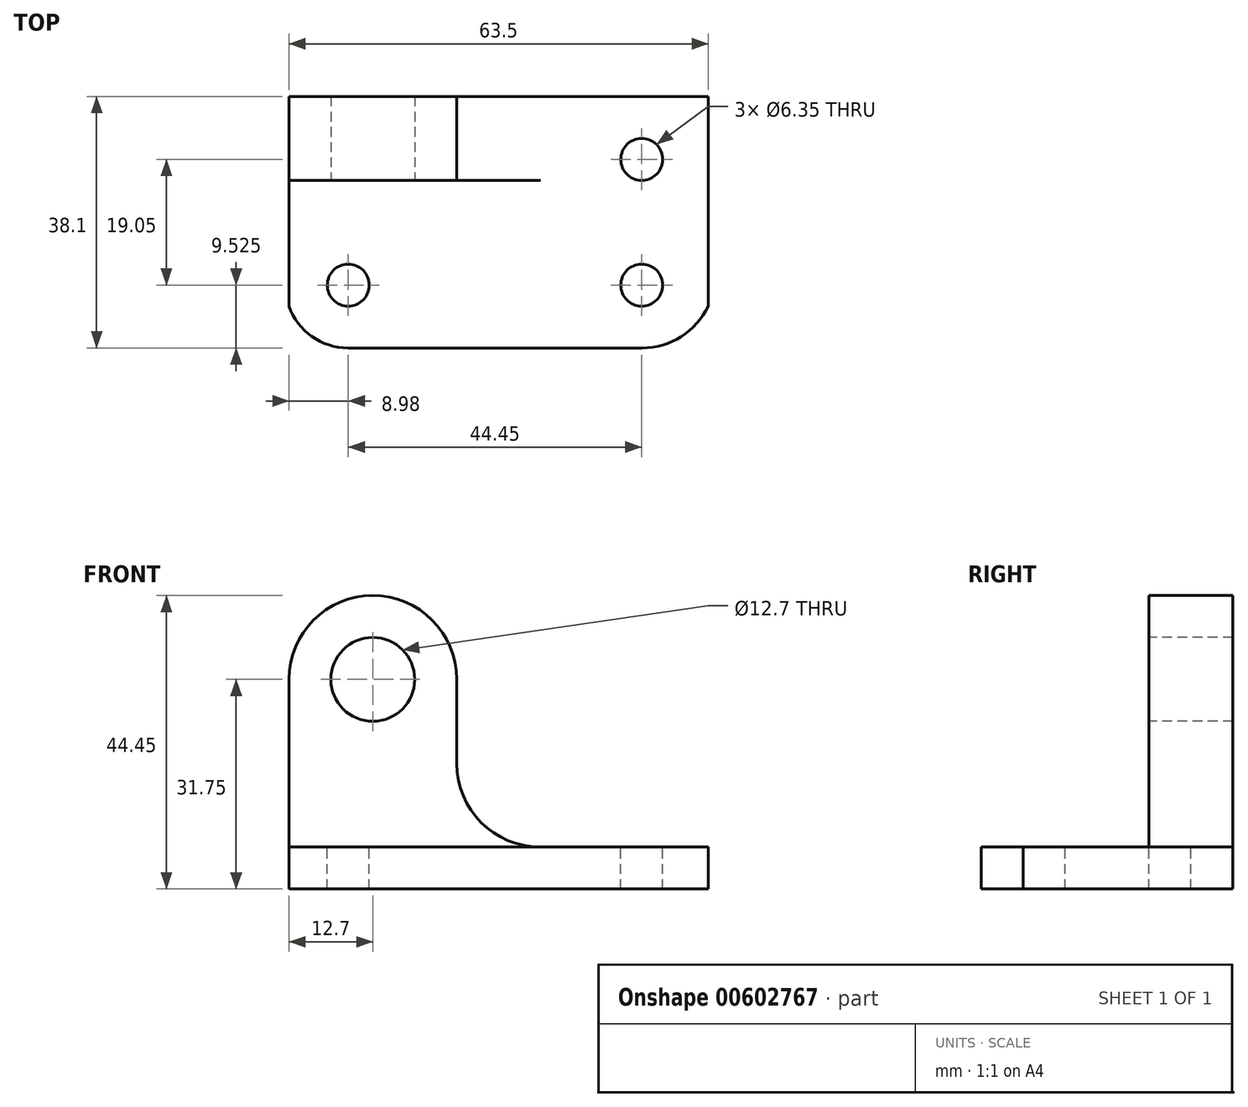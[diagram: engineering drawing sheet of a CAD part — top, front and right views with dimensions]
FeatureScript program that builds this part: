
annotation { "Feature Type Name" : "Feature", "Feature Type Description" : "" }
export const myFeature = defineFeature(function(context is Context, id is Id, definition is map)
    precondition{}
    {
        {
            var Q0;
            Q0=qCreatedBy(makeId("Front.planeOp"),FACE);
            var sketch = newSketch(context, id + "F0", { "sketchPlane" : qUnion([Q0])});
            skLineSegment(sketch, "E0", {"start": v(0, 0) * mm, "end": v(63.5, 0) * mm});
            skLineSegment(sketch, "E1", {"start": v(63.5, 0) * mm, "end": v(63.5, 6.35) * mm});
            skLineSegment(sketch, "E2", {"start": v(63.5, 6.35) * mm, "end": v(38.1, 6.35) * mm});
            skLineSegment(sketch, "E3", {"start": v(38.1, 6.35) * mm, "end": v(38.1, 44.45) * mm});
            skLineSegment(sketch, "E4", {"start": v(38.1, 44.45) * mm, "end": v(0, 44.45) * mm});
            skLineSegment(sketch, "E5", {"start": v(0, 44.45) * mm, "end": v(0, 0) * mm});
            skSolve(sketch);
        }
        {
            var Q0;
            Q0=makeQuery(id+"F0.imprint","IMPRINT",FACE,{"disambiguationData":[TD([[makeQuery(id+"F0.imprint","IMPRINT",EDGE,{"derivedFrom":sQuery(id+"F0.wireOp",EDGE,"E0")}),1.0]])]});
            var sketch = newSketch(context, id + "F1", { "sketchPlane" : qUnion([Q0])});
            skLineSegment(sketch, "E6.0.0", {"start": v(38.1, 44.45) * mm, "end": v(0, 44.45) * mm});
            skLineSegment(sketch, "E6.0.1", {"start": v(0, 44.45) * mm, "end": v(0, 0) * mm});
            skLineSegment(sketch, "E6.0.2", {"start": v(0, 0) * mm, "end": v(63.5, 0) * mm});
            skLineSegment(sketch, "E6.0.3", {"start": v(63.5, 0) * mm, "end": v(63.5, 6.35) * mm});
            skLineSegment(sketch, "E6.0.4", {"start": v(63.5, 6.35) * mm, "end": v(38.1, 6.35) * mm});
            skLineSegment(sketch, "E6.0.5", {"start": v(38.1, 6.35) * mm, "end": v(38.1, 44.45) * mm});
            skArc(sketch, "E7", {"start": v(25.4, 31.75) * mm, "mid": v(12.7, 44.45) * mm, "end": v(0, 31.75) * mm});
            skLineSegment(sketch, "E8", {"start": v(25.4, 31.75) * mm, "end": v(25.4, 19.05) * mm});
            skArc(sketch, "E9", {"start": v(25.4, 19.05) * mm, "mid": v(29.12, 10.07) * mm, "end": v(38.1, 6.35) * mm});
            skSolve(sketch);
        }
        {
            var Q0;
            Q0=makeQuery(id+"F0.imprint","IMPRINT",FACE,{"disambiguationData":[TD([[makeQuery(id+"F0.imprint","IMPRINT",EDGE,{"derivedFrom":sQuery(id+"F0.wireOp",EDGE,"E0")}),1.0]])]});
            var sketch = newSketch(context, id + "F2", { "sketchPlane" : qUnion([Q0])});
            skLineSegment(sketch, "E10.0.0", {"start": v(38.1, 44.45) * mm, "end": v(0, 44.45) * mm});
            skLineSegment(sketch, "E10.0.1", {"start": v(0, 44.45) * mm, "end": v(0, 0) * mm});
            skLineSegment(sketch, "E10.0.2", {"start": v(0, 0) * mm, "end": v(63.5, 0) * mm});
            skLineSegment(sketch, "E10.0.3", {"start": v(63.5, 0) * mm, "end": v(63.5, 6.35) * mm});
            skLineSegment(sketch, "E10.0.4", {"start": v(63.5, 6.35) * mm, "end": v(38.1, 6.35) * mm});
            skLineSegment(sketch, "E10.0.5", {"start": v(38.1, 6.35) * mm, "end": v(38.1, 44.45) * mm});
            skLineSegment(sketch, "E11", {"start": v(38.1, 6.35) * mm, "end": v(0, 6.35) * mm});
            skSolve(sketch);
        }
        {
            var Q0;
            Q0=makeQuery(id+"F0.imprint","IMPRINT",FACE,{"disambiguationData":[TD([[makeQuery(id+"F0.imprint","IMPRINT",EDGE,{"derivedFrom":sQuery(id+"F0.wireOp",EDGE,"E0")}),1.0]])]});
            extrude(context, id + "F3", {"entities" : qUnion([Q0]), "oppositeDirection" : true, "depth" : 38.1 * mm, "offsetDistance" : 25.4 * mm});
        }
        {
            var Q0;
            {var subQ4=sQuery(id+"F1.wireOp",EDGE,"E6.0.5");Q0=makeQuery(id+"F1.imprint","IMPRINT",FACE,{"disambiguationData":[TD([[makeQuery(id+"F1.imprint","IMPRINT",EDGE,{"derivedFrom":subQ4}),1.0]])]});}
            var Q1;
            {var subQ0=sQuery(id+"F1.wireOp",EDGE,"E6.0.1");var subQ1=sQuery(id+"F1.wireOp",EDGE,"E6.0.0");var subQ2=makeQuery(id+"F1.imprint","INTERSECT",VERTEX,{"derivedFrom":[subQ1,subQ0]});Q1=makeQuery(id+"F1.imprint","IMPRINT",FACE,{"disambiguationData":[TD([[makeQuery(id+"F1.imprint","IMPRINT",EDGE,{"disambiguationData":[TD([[subQ2,1.0]])],"derivedFrom":subQ1}),1.0]])]});}
            extrude(context, id + "F4", {"entities" : qUnion([Q0, Q1]), "operationType" : NewBodyOperationType.REMOVE, "oppositeDirection" : true, "depth" : 38.1 * mm, "offsetDistance" : 25.4 * mm});
        }
        {
            var Q0;
            {var subQ0=sQuery(id+"F2.wireOp",EDGE,"E10.0.0");Q0=makeQuery(id+"F2.imprint","IMPRINT",FACE,{"disambiguationData":[TD([[makeQuery(id+"F2.imprint","IMPRINT",EDGE,{"derivedFrom":subQ0}),1.0]])]});}
            extrude(context, id + "F5", {"entities" : qUnion([Q0]), "operationType" : NewBodyOperationType.REMOVE, "oppositeDirection" : true, "depth" : 25.4 * mm, "offsetDistance" : 25.4 * mm});
        }
        {
            var Q0;
            Q0=makeQuery(id+"F5.boolean.opBoolean","MERGE",FACE,{"derivedFrom":[makeQuery(id+"F3.opExtrude","SWEPT_FACE",FACE,{"disambiguationData":[OSD([sQuery(id+"F0.wireOp",EDGE,"E2")])]}),makeQuery(id+"F5.opExtrude","SWEPT_FACE",FACE,{"disambiguationData":[OSD([sQuery(id+"F2.wireOp",EDGE,"E11")])]})]});
            var sketch = newSketch(context, id + "F6", { "sketchPlane" : qUnion([Q0])});
            skLineSegment(sketch, "E12.0.0", {"start": v(0, 0) * mm, "end": v(63.5, 0) * mm});
            skLineSegment(sketch, "E12.0.1", {"start": v(63.5, 0) * mm, "end": v(63.5, 38.1) * mm});
            skLineSegment(sketch, "E12.0.2", {"start": v(63.5, 38.1) * mm, "end": v(38.1, 38.1) * mm});
            skLineSegment(sketch, "E12.0.3", {"start": v(38.1, 38.1) * mm, "end": v(38.1, 25.4) * mm});
            skLineSegment(sketch, "E12.0.4", {"start": v(38.1, 25.4) * mm, "end": v(0, 25.4) * mm});
            skLineSegment(sketch, "E12.0.5", {"start": v(0, 25.4) * mm, "end": v(0, 0) * mm});
            skArc(sketch, "E13", {"start": v(0, 6.35) * mm, "mid": v(3.46, 1.76) * mm, "end": v(8.94, 0) * mm});
            skArc(sketch, "E14", {"start": v(53.39, 0) * mm, "mid": v(59.36, 1.7) * mm, "end": v(63.5, 6.35) * mm});
            skSolve(sketch);
        }
        {
            var Q0;
            {var subQ3=sQuery(id+"F6.wireOp",EDGE,"E13");Q0=makeQuery(id+"F6.imprint","IMPRINT",FACE,{"disambiguationData":[TD([[makeQuery(id+"F6.imprint","IMPRINT",EDGE,{"derivedFrom":subQ3}),-1.0]])]});}
            var Q1;
            {var subQ0=sQuery(id+"F6.wireOp",EDGE,"E12.0.1");var subQ1=sQuery(id+"F6.wireOp",EDGE,"E12.0.0");var subQ2=makeQuery(id+"F6.imprint","INTERSECT",VERTEX,{"derivedFrom":[subQ1,subQ0]});Q1=makeQuery(id+"F6.imprint","IMPRINT",FACE,{"disambiguationData":[TD([[makeQuery(id+"F6.imprint","IMPRINT",EDGE,{"disambiguationData":[TD([[subQ2,-1.0]])],"derivedFrom":subQ1}),-1.0]])]});}
            extrude(context, id + "F7", {"entities" : qUnion([Q0, Q1]), "operationType" : NewBodyOperationType.REMOVE, "oppositeDirection" : true, "depth" : 6.35 * mm, "offsetDistance" : 25.4 * mm});
        }
        {
            var Q0;
            Q0=makeQuery(id+"F5.boolean.opBoolean","COPY",FACE,{"derivedFrom":makeQuery(id+"F5.opExtrude","CAP_FACE",FACE,{"disambiguationData":[OSD([sQuery(id+"F2.wireOp",EDGE,"E10.0.0"),sQuery(id+"F2.wireOp",EDGE,"E10.0.1"),sQuery(id+"F2.wireOp",EDGE,"E10.0.5"),sQuery(id+"F2.wireOp",EDGE,"E11")])],"isStart":false})});
            var sketch = newSketch(context, id + "F8", { "sketchPlane" : qUnion([Q0])});
            skCircle(sketch, "E15", {"center": v(12.7, 31.75) * mm, "radius": 6.35 * mm});
            skSolve(sketch);
        }
        {
            var Q0;
            Q0=makeQuery(id+"F8.imprint","IMPRINT",FACE,{"disambiguationData":[TD([[makeQuery(id+"F8.imprint","IMPRINT",EDGE,{"derivedFrom":sQuery(id+"F8.wireOp",EDGE,"E15")}),1.0]])]});
            extrude(context, id + "F9", {"entities" : qUnion([Q0]), "operationType" : NewBodyOperationType.REMOVE, "oppositeDirection" : true, "depth" : 12.7 * mm, "offsetDistance" : 25.4 * mm});
        }
        {
            var Q0;
            Q0=makeQuery(id+"F5.boolean.opBoolean","MERGE",FACE,{"derivedFrom":[makeQuery(id+"F3.opExtrude","SWEPT_FACE",FACE,{"disambiguationData":[OSD([sQuery(id+"F0.wireOp",EDGE,"E2")])]}),makeQuery(id+"F5.opExtrude","SWEPT_FACE",FACE,{"disambiguationData":[OSD([sQuery(id+"F2.wireOp",EDGE,"E11")])]})]});
            var sketch = newSketch(context, id + "F10", { "sketchPlane" : qUnion([Q0])});
            skCircle(sketch, "E16", {"center": v(8.98, 9.52) * mm, "radius": 3.17 * mm});
            skCircle(sketch, "E17", {"center": v(53.43, 9.52) * mm, "radius": 3.18 * mm});
            skCircle(sketch, "E18", {"center": v(53.43, 28.58) * mm, "radius": 3.18 * mm});
            skSolve(sketch);
        }
        {
            var Q0;
            Q0=makeQuery(id+"F10.imprint","IMPRINT",FACE,{"disambiguationData":[TD([[makeQuery(id+"F10.imprint","IMPRINT",EDGE,{"derivedFrom":sQuery(id+"F10.wireOp",EDGE,"E16")}),1.0]])]});
            var Q1;
            Q1=makeQuery(id+"F10.imprint","IMPRINT",FACE,{"disambiguationData":[TD([[makeQuery(id+"F10.imprint","IMPRINT",EDGE,{"derivedFrom":sQuery(id+"F10.wireOp",EDGE,"E17")}),1.0]])]});
            var Q2;
            Q2=makeQuery(id+"F10.imprint","IMPRINT",FACE,{"disambiguationData":[TD([[makeQuery(id+"F10.imprint","IMPRINT",EDGE,{"derivedFrom":sQuery(id+"F10.wireOp",EDGE,"E18")}),1.0]])]});
            extrude(context, id + "F11", {"entities" : qUnion([Q0, Q1, Q2]), "operationType" : NewBodyOperationType.REMOVE, "oppositeDirection" : true, "depth" : 6.35 * mm, "offsetDistance" : 25.4 * mm});
        }
    });
